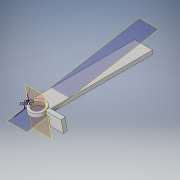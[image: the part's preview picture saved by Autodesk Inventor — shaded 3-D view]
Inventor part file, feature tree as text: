
AUTODESK INVENTOR PART (.ipt)
format: ipt  version: 2017 (Build 210142000, 142)  size: 154,624 bytes
history: native  units: in
note: dims shown in document units (in); Inventor stores cm internally (conversion verified against a paired STEP export)
features: sketch x5, projected_geometry x5, extrude x3, plane x2, hole x1
ambient origin geometry x8: Origin, YZ Plane, XZ Plane, XY Plane, X Axis, Y Axis, Z Axis, Center Point
bodies: Solid1 (feature_tree)
feature tree (16):
  extrude  "Extrusion1"  Depth=5.0in
  sketch  "Sketch2"  dims[d2=0.1875in d3=0.0in d4=0.6871in]
  plane  "Work Plane1"
  extrude  "Extrusion2"  Depth=0.1875in
  hole  "Hole2"  [1 undecoded]
  plane  "Work Plane3"
  extrude  "Extrusion3"  Depth=0.1875in TaperAngle=0.0deg
  sketch  "Sketch1"  dims[d0=0.85in d1=5.0in]
  sketch  "Sketch3"  dims[d5=0.75in d6=0.85in]
  projected_geometry  "Projected Loop1"
  projected_geometry  "Projected Loop2"
  sketch  "Sketch5"  dims[d7=0.425in d8=0.1875in d9=0.0in]
  projected_geometry  "Projected Loop4"
  sketch  "Sketch7"  dims[d17=0.51in d18=0.75in d19=0.375in d20=0.25in d21=0.5635in d22=1.0in d23=0.8108in d24=0.0687in d25=90.0deg d26=0.75in d27=0.625in d28=0.625in d29=0.1875in d30=0.0in]
  projected_geometry  "Projected Loop7"
  projected_geometry  "Projected Loop8"
note: 1 required parameter value undecoded (feature->parameter linkage not recoverable at this tier; creation-order binding heuristic only, values carry confidence <= 0.55)
